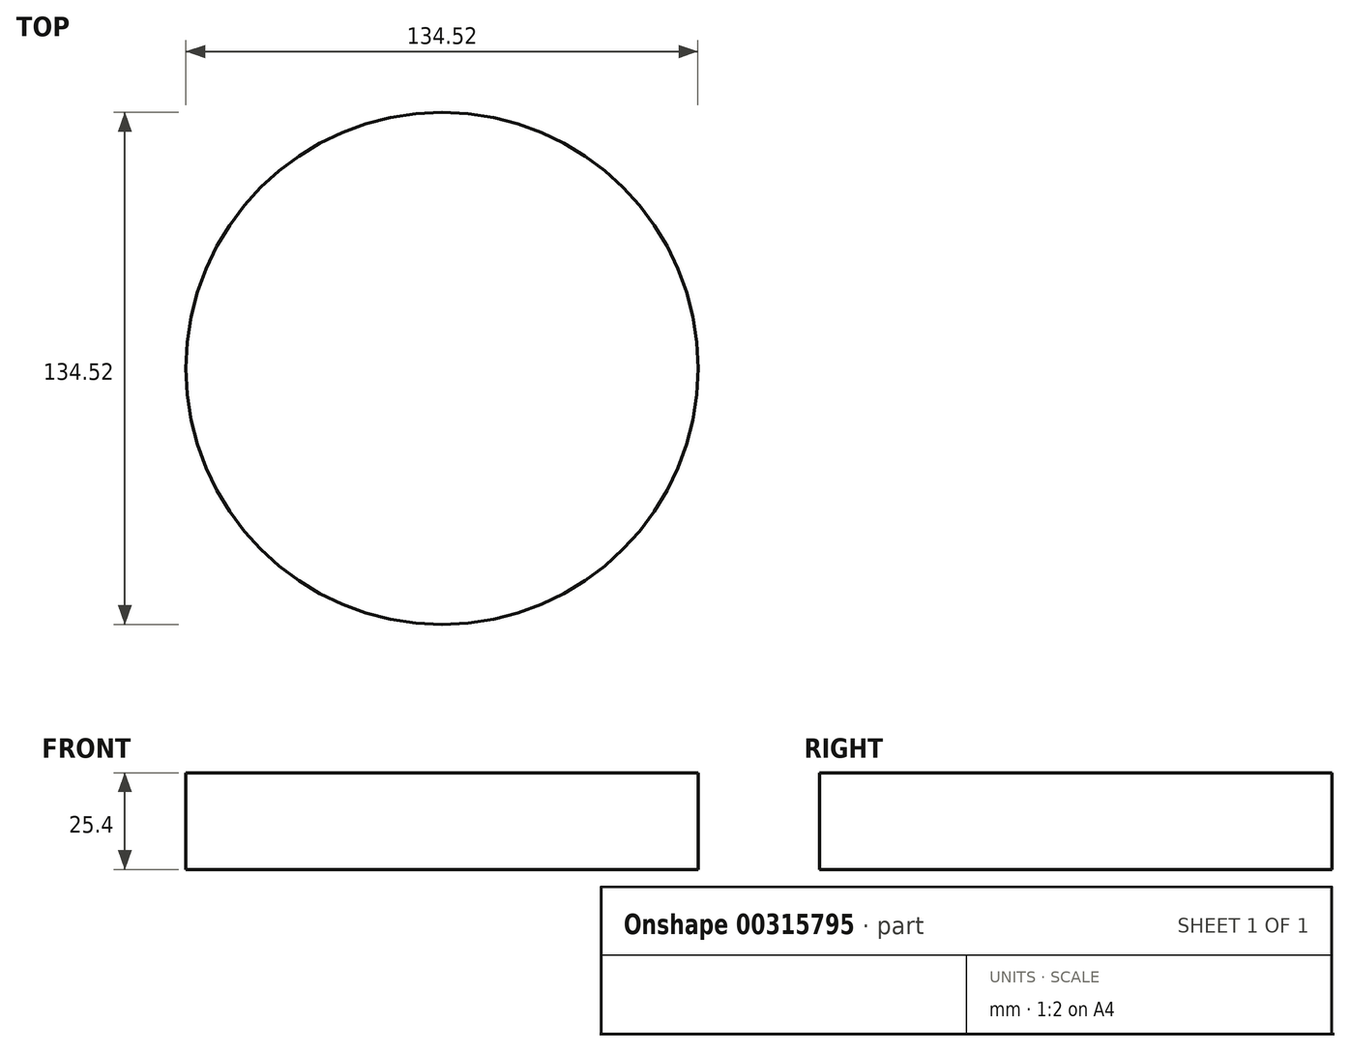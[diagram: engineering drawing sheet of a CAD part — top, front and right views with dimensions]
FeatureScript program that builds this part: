
annotation { "Feature Type Name" : "Feature", "Feature Type Description" : "" }
export const myFeature = defineFeature(function(context is Context, id is Id, definition is map)
    precondition{}
    {
        {
            var Q0;
            Q0=qCreatedBy(makeId("Top.planeOp"),FACE);
            var sketch = newSketch(context, id + "F0", { "sketchPlane" : qUnion([Q0])});
            skCircle(sketch, "E0", {"center": v(0, 0) * mm, "radius": 67.26 * mm});
            skSolve(sketch);
        }
        {
            var Q0;
            Q0 = qSketchRegion(id + "F0", true);
            extrude(context, id + "F1", {"entities" : qUnion([Q0]), "depth" : 25.4 * mm});
        }
    });
